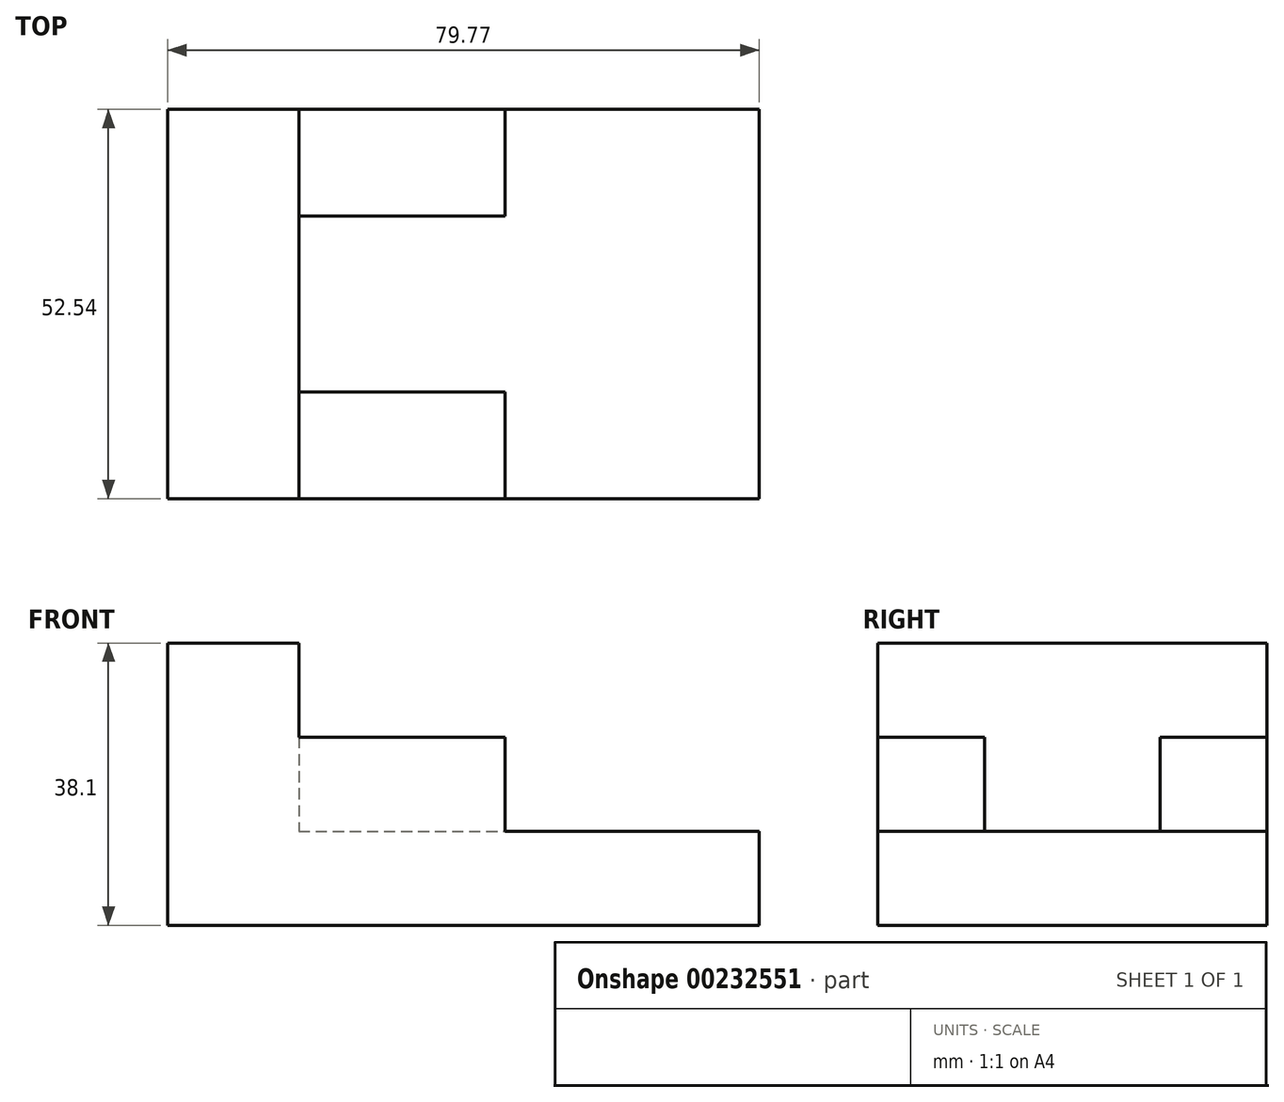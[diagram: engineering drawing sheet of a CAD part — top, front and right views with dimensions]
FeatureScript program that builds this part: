
annotation { "Feature Type Name" : "Feature", "Feature Type Description" : "" }
export const myFeature = defineFeature(function(context is Context, id is Id, definition is map)
    precondition{}
    {
        {
            var Q0;
            Q0=qCreatedBy(makeId("Top.planeOp"),FACE);
            var sketch = newSketch(context, id + "F0", { "sketchPlane" : qUnion([Q0])});
            skLineSegment(sketch, "E0.bottom", {"start": v(0, 0) * mm, "end": v(79.77, 0) * mm});
            skLineSegment(sketch, "E0.top", {"start": v(0, 52.54) * mm, "end": v(79.77, 52.54) * mm});
            skLineSegment(sketch, "E0.left", {"start": v(0, 0) * mm, "end": v(0, 52.54) * mm});
            skLineSegment(sketch, "E0.right", {"start": v(79.77, 0) * mm, "end": v(79.77, 52.54) * mm});
            skSolve(sketch);
        }
        {
            var Q0;
            Q0=makeQuery(id+"F0.imprint","IMPRINT",FACE,{"disambiguationData":[TD([[makeQuery(id+"F0.imprint","IMPRINT",EDGE,{"derivedFrom":sQuery(id+"F0.wireOp",EDGE,"E0.bottom")}),1.0]])]});
            extrude(context, id + "F1", {"entities" : qUnion([Q0]), "depth" : 12.7 * mm});
        }
        {
            var Q0;
            Q0=makeQuery(id+"F1.opExtrude","CAP_FACE",FACE,{"disambiguationData":[OSD([sQuery(id+"F0.wireOp",EDGE,"E0.bottom"),sQuery(id+"F0.wireOp",EDGE,"E0.top"),sQuery(id+"F0.wireOp",EDGE,"E0.left"),sQuery(id+"F0.wireOp",EDGE,"E0.right")])],"isStart":false});
            var sketch = newSketch(context, id + "F2", { "sketchPlane" : qUnion([Q0])});
            skLineSegment(sketch, "E1.bottom", {"start": v(0, 52.54) * mm, "end": v(17.67, 52.54) * mm});
            skLineSegment(sketch, "E1.top", {"start": v(0, 0) * mm, "end": v(17.67, 0) * mm});
            skLineSegment(sketch, "E1.left", {"start": v(0, 52.54) * mm, "end": v(0, 0) * mm});
            skLineSegment(sketch, "E1.right", {"start": v(17.67, 52.54) * mm, "end": v(17.67, 0) * mm});
            skLineSegment(sketch, "E2.bottom", {"start": v(17.67, 0) * mm, "end": v(45.48, 0) * mm});
            skLineSegment(sketch, "E2.top", {"start": v(17.67, 14.4) * mm, "end": v(45.48, 14.4) * mm});
            skLineSegment(sketch, "E2.left", {"start": v(17.67, 0) * mm, "end": v(17.67, 14.4) * mm});
            skLineSegment(sketch, "E2.right", {"start": v(45.48, 0) * mm, "end": v(45.48, 14.4) * mm});
            skLineSegment(sketch, "E3.bottom", {"start": v(17.67, 52.54) * mm, "end": v(45.48, 52.54) * mm});
            skLineSegment(sketch, "E3.top", {"start": v(17.67, 38.14) * mm, "end": v(45.48, 38.14) * mm});
            skLineSegment(sketch, "E3.left", {"start": v(17.67, 52.54) * mm, "end": v(17.67, 38.14) * mm});
            skLineSegment(sketch, "E3.right", {"start": v(45.48, 52.54) * mm, "end": v(45.48, 38.14) * mm});
            skSolve(sketch);
        }
        {
            var Q0;
            Q0=makeQuery(id+"F2.imprint","IMPRINT",FACE,{"disambiguationData":[TD([[makeQuery(id+"F2.imprint","IMPRINT",EDGE,{"derivedFrom":sQuery(id+"F2.wireOp",EDGE,"E1.bottom")}),-1.0]])]});
            var Q1;
            Q1=makeQuery(id+"F2.imprint","IMPRINT",FACE,{"disambiguationData":[TD([[makeQuery(id+"F2.imprint","IMPRINT",EDGE,{"derivedFrom":sQuery(id+"F2.wireOp",EDGE,"E2.bottom")}),1.0]])]});
            var Q2;
            Q2=makeQuery(id+"F2.imprint","IMPRINT",FACE,{"disambiguationData":[TD([[makeQuery(id+"F2.imprint","IMPRINT",EDGE,{"derivedFrom":sQuery(id+"F2.wireOp",EDGE,"E3.bottom")}),-1.0]])]});
            extrude(context, id + "F3", {"entities" : qUnion([Q0, Q1, Q2]), "operationType" : NewBodyOperationType.ADD, "depth" : 12.7 * mm});
        }
        {
            var Q0;
            Q0=makeQuery(id+"F3.opExtrude","CAP_FACE",FACE,{"disambiguationData":[OSD([sQuery(id+"F2.wireOp",EDGE,"E1.bottom"),sQuery(id+"F2.wireOp",EDGE,"E1.top"),sQuery(id+"F2.wireOp",EDGE,"E1.left"),sQuery(id+"F2.wireOp",EDGE,"E1.right"),sQuery(id+"F2.wireOp",EDGE,"E2.bottom"),sQuery(id+"F2.wireOp",EDGE,"E2.top"),sQuery(id+"F2.wireOp",EDGE,"E2.right"),sQuery(id+"F2.wireOp",EDGE,"E3.bottom"),sQuery(id+"F2.wireOp",EDGE,"E3.top"),sQuery(id+"F2.wireOp",EDGE,"E3.right")])],"isStart":false});
            var sketch = newSketch(context, id + "F4", { "sketchPlane" : qUnion([Q0])});
            skLineSegment(sketch, "E4.bottom", {"start": v(0, 52.54) * mm, "end": v(17.67, 52.54) * mm});
            skLineSegment(sketch, "E4.top", {"start": v(0, 0) * mm, "end": v(17.67, 0) * mm});
            skLineSegment(sketch, "E4.left", {"start": v(0, 52.54) * mm, "end": v(0, 0) * mm});
            skLineSegment(sketch, "E4.right", {"start": v(17.67, 52.54) * mm, "end": v(17.67, 0) * mm});
            skSolve(sketch);
        }
        {
            var Q0;
            {var subQ2=sQuery(id+"F4.wireOp",EDGE,"E4.bottom");Q0=makeQuery(id+"F4.imprint","IMPRINT",FACE,{"disambiguationData":[TD([[makeQuery(id+"F4.imprint","IMPRINT",EDGE,{"derivedFrom":subQ2}),-1.0]])]});}
            extrude(context, id + "F5", {"entities" : qUnion([Q0]), "operationType" : NewBodyOperationType.ADD, "depth" : 12.7 * mm});
        }
    });
